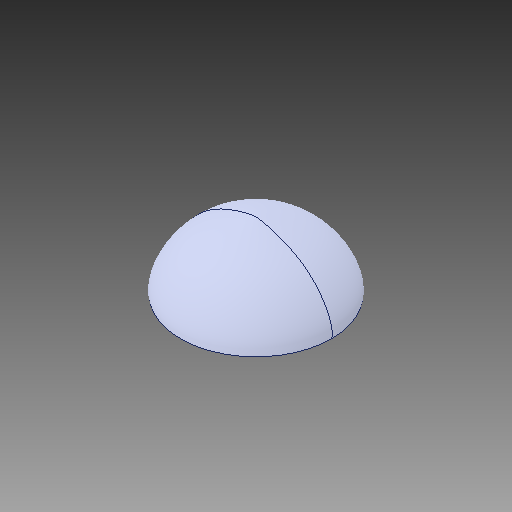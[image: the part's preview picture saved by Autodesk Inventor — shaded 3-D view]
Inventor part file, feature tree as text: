
AUTODESK INVENTOR PART (.ipt)
format: ipt  version: 2019.4 (Build 234330000, 330)  size: 120,832 bytes
history: native  units: in
note: dims shown in document units (in); Inventor stores cm internally (conversion verified against a paired STEP export)
features: revolve x1
ambient origin geometry x8: Origin, YZ Plane, XZ Plane, XY Plane, X Axis, Y Axis, Z Axis, Center Point
bodies: Solid1 (feature_tree)
feature tree (1):
  revolve  "Revolve1"  [1 undecoded]
note: 1 required parameter value undecoded (feature->parameter linkage not recoverable at this tier; creation-order binding heuristic only, values carry confidence <= 0.55)
